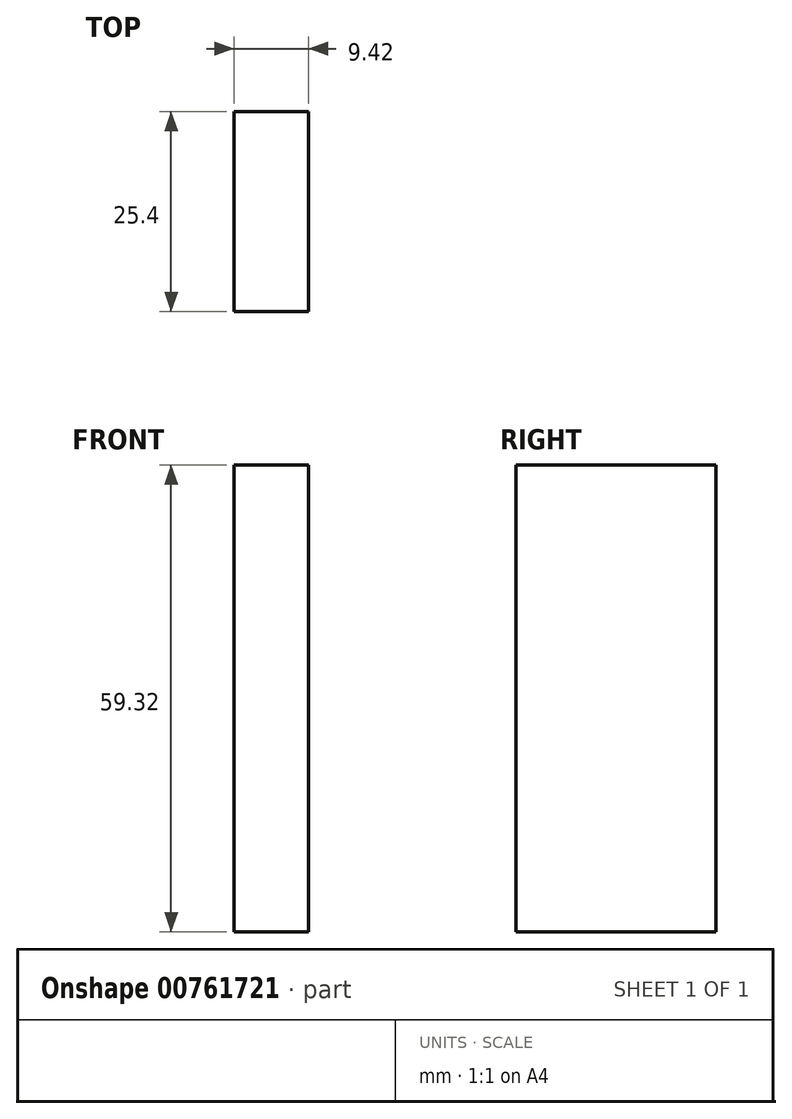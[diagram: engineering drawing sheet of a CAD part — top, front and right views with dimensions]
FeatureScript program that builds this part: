
annotation { "Feature Type Name" : "Feature", "Feature Type Description" : "" }
export const myFeature = defineFeature(function(context is Context, id is Id, definition is map)
    precondition{}
    {
        {
            var Q0;
            Q0=qCreatedBy(makeId("Front.planeOp"),FACE);
            var sketch = newSketch(context, id + "F0", { "sketchPlane" : qUnion([Q0])});
            skLineSegment(sketch, "E0", {"start": v(0, 0) * mm, "end": v(0, -59.32) * mm});
            skLineSegment(sketch, "E1", {"start": v(0, -59.32) * mm, "end": v(9.42, -59.32) * mm});
            skLineSegment(sketch, "E2", {"start": v(9.42, -59.32) * mm, "end": v(9.42, 0) * mm});
            skLineSegment(sketch, "E3", {"start": v(9.42, 0) * mm, "end": v(0, 0) * mm});
            skSolve(sketch);
        }
        {
            var Q0;
            Q0=makeQuery(id+"F0.imprint","IMPRINT",FACE,{"disambiguationData":[TD([[makeQuery(id+"F0.imprint","IMPRINT",EDGE,{"derivedFrom":sQuery(id+"F0.wireOp",EDGE,"E0")}),1.0]])]});
            extrude(context, id + "F1", {"entities" : qUnion([Q0]), "depth" : 25.4 * mm, "offsetDistance" : 25.4 * mm});
        }
    });
